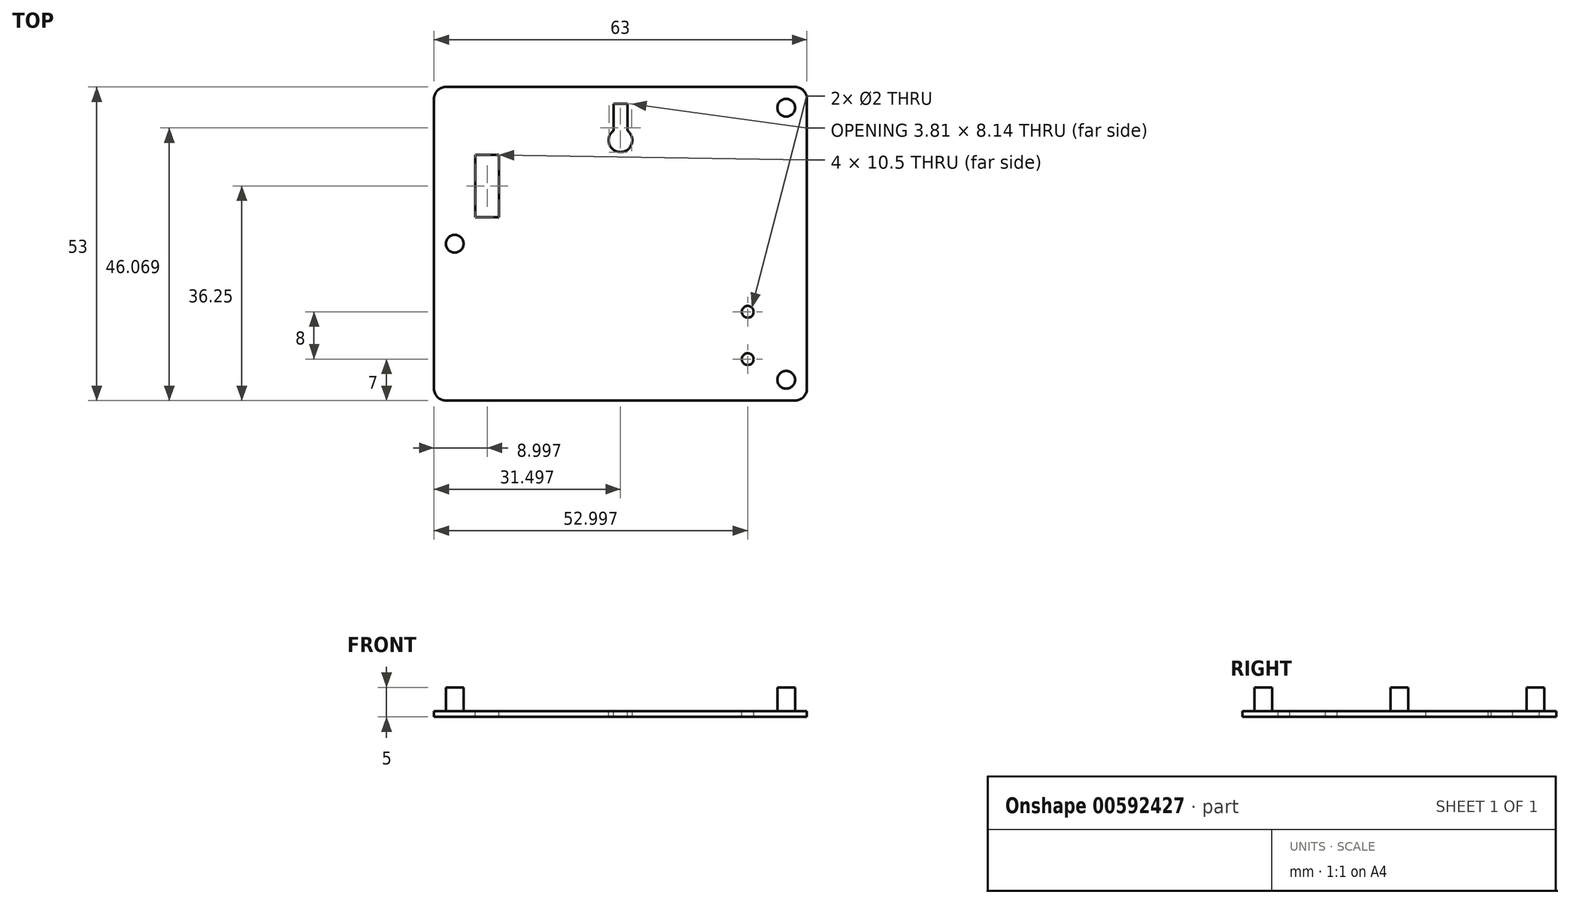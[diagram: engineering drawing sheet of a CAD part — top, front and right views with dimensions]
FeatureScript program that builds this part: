
annotation { "Feature Type Name" : "Feature", "Feature Type Description" : "" }
export const myFeature = defineFeature(function(context is Context, id is Id, definition is map)
    precondition{}
    {
        {
            var Q0;
            Q0=qCreatedBy(makeId("Top.planeOp"),FACE);
            var sketch = newSketch(context, id + "F0", { "sketchPlane" : qUnion([Q0])});
            skLineSegment(sketch, "E0.bottom", {"start": v(-8.2, 0) * mm, "end": v(-71.2, 0) * mm});
            skLineSegment(sketch, "E0.top", {"start": v(-8.2, 53) * mm, "end": v(-71.2, 53) * mm});
            skLineSegment(sketch, "E0.left", {"start": v(-8.2, 0) * mm, "end": v(-8.2, 53) * mm});
            skLineSegment(sketch, "E0.right", {"start": v(-71.2, 0) * mm, "end": v(-71.2, 53) * mm});
            skPoint(sketch, "E0.middle", {"position": v(-39.7, 26.5) * mm});
            skSolve(sketch);
        }
        {
            var Q0;
            Q0=makeQuery(id+"F0.imprint","IMPRINT",FACE,{"disambiguationData":[TD([[makeQuery(id+"F0.imprint","IMPRINT",EDGE,{"derivedFrom":sQuery(id+"F0.wireOp",EDGE,"E0.bottom")}),-1.0]])]});
            var sketch = newSketch(context, id + "F1", { "sketchPlane" : qUnion([Q0])});
            skCircle(sketch, "E1", {"center": v(-11.7, 49.5) * mm, "radius": 1.5 * mm});
            skCircle(sketch, "E2", {"center": v(-11.7, 3.5) * mm, "radius": 1.5 * mm});
            skCircle(sketch, "E3", {"center": v(-67.7, 26.5) * mm, "radius": 1.5 * mm});
            skLineSegment(sketch, "E4.bottom", {"start": v(-64.2, 41.5) * mm, "end": v(-60.2, 41.5) * mm});
            skLineSegment(sketch, "E4.top", {"start": v(-64.2, 31) * mm, "end": v(-60.2, 31) * mm});
            skLineSegment(sketch, "E4.left", {"start": v(-64.2, 41.5) * mm, "end": v(-64.2, 31) * mm});
            skLineSegment(sketch, "E4.right", {"start": v(-60.2, 41.5) * mm, "end": v(-60.2, 31) * mm});
            skPoint(sketch, "E4.middle", {"position": v(-62.2, 36.25) * mm});
            skCircle(sketch, "E5", {"center": v(-18.2, 7) * mm, "radius": 1 * mm});
            skCircle(sketch, "E6", {"center": v(-18.2, 15) * mm, "radius": 1 * mm});
            skCircle(sketch, "E7", {"center": v(-39.7, 44) * mm, "radius": 2 * mm});
            skLineSegment(sketch, "E8.bottom", {"start": v(-38.53, 45.62) * mm, "end": v(-40.87, 45.62) * mm});
            skLineSegment(sketch, "E8.top", {"start": v(-38.53, 50.14) * mm, "end": v(-40.87, 50.14) * mm});
            skLineSegment(sketch, "E8.left", {"start": v(-38.53, 45.62) * mm, "end": v(-38.53, 50.14) * mm});
            skLineSegment(sketch, "E8.right", {"start": v(-40.87, 45.62) * mm, "end": v(-40.87, 50.14) * mm});
            skPoint(sketch, "E8.middle", {"position": v(-39.7, 47.88) * mm});
            skSolve(sketch);
        }
        {
            var Q0;
            Q0=makeQuery(id+"F1.imprint","IMPRINT",FACE,{"disambiguationData":[TD([[makeQuery(id+"F1.imprint","IMPRINT",EDGE,{"derivedFrom":sQuery(id+"F1.wireOp",EDGE,"E1")}),-1.0]])]});
            extrude(context, id + "F2", {"entities" : qUnion([Q0]), "depth" : 1 * mm, "offsetDistance" : 25 * mm});
        }
        {
            var Q0;
            Q0=makeQuery(id+"F2.opExtrude","SWEPT_EDGE",EDGE,{"disambiguationData":[OSD([sQuery(id+"F0.wireOp",EDGE,"E0.top"),sQuery(id+"F0.wireOp",EDGE,"E0.right")])]});
            var Q1;
            Q1=makeQuery(id+"F2.opExtrude","SWEPT_EDGE",EDGE,{"disambiguationData":[OSD([sQuery(id+"F0.wireOp",EDGE,"E0.bottom"),sQuery(id+"F0.wireOp",EDGE,"E0.right")])]});
            var Q2;
            Q2=makeQuery(id+"F2.opExtrude","SWEPT_EDGE",EDGE,{"disambiguationData":[OSD([sQuery(id+"F0.wireOp",EDGE,"E0.bottom"),sQuery(id+"F0.wireOp",EDGE,"E0.left")])]});
            var Q3;
            Q3=makeQuery(id+"F2.opExtrude","SWEPT_EDGE",EDGE,{"disambiguationData":[OSD([sQuery(id+"F0.wireOp",EDGE,"E0.top"),sQuery(id+"F0.wireOp",EDGE,"E0.left")])]});
            fillet(context, id + "F3", {"entities" : qUnion([Q0, Q1, Q2, Q3]), "radius" : 2 * mm, "tangentPropagation" : true, "allowEdgeOverflow" : false});
        }
        {
            var Q0;
            Q0 = qSketchRegion(id + "F1", true);
            extrude(context, id + "F4", {"entities" : qUnion([Q0]), "operationType" : NewBodyOperationType.ADD, "depth" : 25 * mm, "offsetDistance" : 25 * mm});
        }
        {
            var Q0;
            Q0=makeQuery(id+"F4.opExtrude","CAP_FACE",FACE,{"disambiguationData":[OSD([sQuery(id+"F1.wireOp",EDGE,"E4.bottom"),sQuery(id+"F1.wireOp",EDGE,"E4.top"),sQuery(id+"F1.wireOp",EDGE,"E4.left"),sQuery(id+"F1.wireOp",EDGE,"E4.right")])],"isStart":false});
            extrude(context, id + "F5", {"entities" : qUnion([Q0]), "operationType" : NewBodyOperationType.REMOVE, "oppositeDirection" : true, "depth" : 25 * mm, "offsetDistance" : 25 * mm});
        }
        {
            var Q0;
            Q0=makeQuery(id+"F4.opExtrude","CAP_FACE",FACE,{"disambiguationData":[OSD([sQuery(id+"F1.wireOp",EDGE,"E7"),sQuery(id+"F1.wireOp",EDGE,"E8.top"),sQuery(id+"F1.wireOp",EDGE,"E8.left"),sQuery(id+"F1.wireOp",EDGE,"E8.right")])],"isStart":false});
            var Q1;
            Q1=makeQuery(id+"F4.opExtrude","CAP_FACE",FACE,{"disambiguationData":[OSD([sQuery(id+"F1.wireOp",EDGE,"E6")])],"isStart":false});
            var Q2;
            Q2=makeQuery(id+"F4.opExtrude","CAP_FACE",FACE,{"disambiguationData":[OSD([sQuery(id+"F1.wireOp",EDGE,"E5")])],"isStart":false});
            extrude(context, id + "F6", {"entities" : qUnion([Q0, Q1, Q2]), "operationType" : NewBodyOperationType.REMOVE, "oppositeDirection" : true, "depth" : 25 * mm, "offsetDistance" : 25 * mm});
        }
        {
            var Q0;
            Q0=makeQuery(id+"F4.opExtrude","CAP_FACE",FACE,{"disambiguationData":[OSD([sQuery(id+"F1.wireOp",EDGE,"E1")])],"isStart":false});
            var Q1;
            Q1=makeQuery(id+"F4.opExtrude","CAP_FACE",FACE,{"disambiguationData":[OSD([sQuery(id+"F1.wireOp",EDGE,"E3")])],"isStart":false});
            var Q2;
            Q2=makeQuery(id+"F4.opExtrude","CAP_FACE",FACE,{"disambiguationData":[OSD([sQuery(id+"F1.wireOp",EDGE,"E2")])],"isStart":false});
            extrude(context, id + "F7", {"entities" : qUnion([Q0, Q1, Q2]), "operationType" : NewBodyOperationType.REMOVE, "oppositeDirection" : true, "depth" : 20 * mm, "offsetDistance" : 25 * mm});
        }
    });
